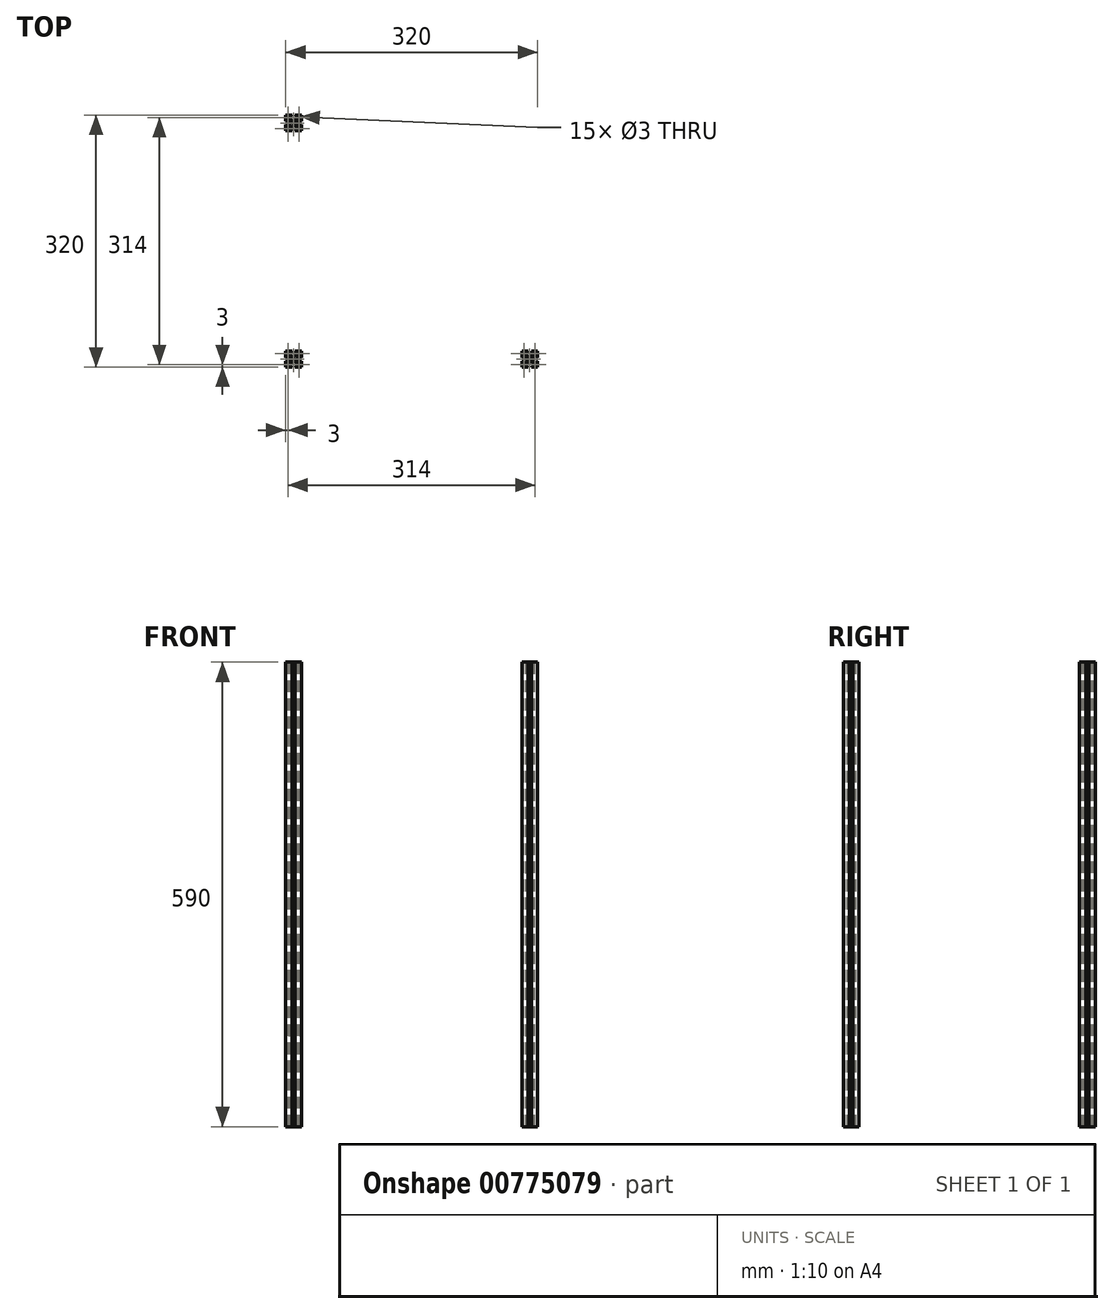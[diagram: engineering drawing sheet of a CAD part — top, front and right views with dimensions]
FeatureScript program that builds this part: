
annotation { "Feature Type Name" : "Feature", "Feature Type Description" : "" }
export const myFeature = defineFeature(function(context is Context, id is Id, definition is map)
    precondition{}
    {
        {
            var Q0;
            Q0=qCreatedBy(makeId("Top.planeOp"),FACE);
            var sketch = newSketch(context, id + "F0", { "sketchPlane" : qUnion([Q0])});
            skLineSegment(sketch, "E0.bottom", {"start": v(-10, 10) * mm, "end": v(-2.15, 10) * mm});
            skLineSegment(sketch, "E0.top", {"start": v(-10, -10) * mm, "end": v(-2.15, -10) * mm});
            skLineSegment(sketch, "E0.left", {"start": v(-10, 10) * mm, "end": v(-10, 2.15) * mm});
            skLineSegment(sketch, "E0.right", {"start": v(10, 10) * mm, "end": v(10, 2.15) * mm});
            skLineSegment(sketch, "E1", {"start": v(-35.32, 0) * mm, "end": v(22.78, 0) * mm, "construction": true});
            skLineSegment(sketch, "E2.0", {"start": v(-10, -7) * mm, "end": v(10, -7) * mm, "construction": true});
            skLineSegment(sketch, "E3.0", {"start": v(-10, 7) * mm, "end": v(10, 7) * mm, "construction": true});
            skLineSegment(sketch, "E4", {"start": v(0, -15.68) * mm, "end": v(0, 21.93) * mm, "construction": true});
            skPoint(sketch, "E4.endSnap0", {"position": v(0, -7) * mm});
            skLineSegment(sketch, "E5.0", {"start": v(7, -10) * mm, "end": v(7, 10) * mm, "construction": true});
            skLineSegment(sketch, "E6.0", {"start": v(-7, -10) * mm, "end": v(-7, 10) * mm, "construction": true});
            skLineSegment(sketch, "E7.0", {"start": v(-4.15, 8.5) * mm, "end": v(-2.15, 8.5) * mm});
            skLineSegment(sketch, "E8.0", {"start": v(-4.15, 4.8) * mm, "end": v(-2.15, 4.8) * mm});
            skLineSegment(sketch, "E9.trimOffspring", {"start": v(2.15, 8.5) * mm, "end": v(2.15, 10) * mm});
            skLineSegment(sketch, "E10.trimOffspring", {"start": v(4.15, 4.8) * mm, "end": v(4.15, 8.5) * mm});
            skLineSegment(sketch, "E11.MirrorCS", {"start": v(-2.15, 8.5) * mm, "end": v(-2.15, 10) * mm});
            skLineSegment(sketch, "E12", {"start": v(-2.15, 3.3) * mm, "end": v(4.15, 4.8) * mm});
            skLineSegment(sketch, "E13.trimOffspring", {"start": v(-2.15, 4.8) * mm, "end": v(-2.15, 3.3) * mm});
            skLineSegment(sketch, "E14.MirrorCS", {"start": v(-4.15, 4.8) * mm, "end": v(-4.15, 8.5) * mm});
            skLineSegment(sketch, "E15.trimOffspring", {"start": v(2.15, 8.5) * mm, "end": v(4.15, 8.5) * mm});
            skLineSegment(sketch, "E16.trimOffspring", {"start": v(2.15, 10) * mm, "end": v(10, 10) * mm});
            skLineSegment(sketch, "E17.1.0", {"start": v(4.8, 4.15) * mm, "end": v(4.8, 2.15) * mm});
            skLineSegment(sketch, "E17.1.1", {"start": v(8.5, 4.15) * mm, "end": v(8.5, 2.15) * mm});
            skLineSegment(sketch, "E17.1.2", {"start": v(3.3, 2.15) * mm, "end": v(4.8, -4.15) * mm});
            skLineSegment(sketch, "E17.1.3", {"start": v(8.5, 2.15) * mm, "end": v(10, 2.15) * mm});
            skLineSegment(sketch, "E17.1.4", {"start": v(4.8, -4.15) * mm, "end": v(8.5, -4.15) * mm});
            skLineSegment(sketch, "E17.1.5", {"start": v(4.8, 4.15) * mm, "end": v(8.5, 4.15) * mm});
            skLineSegment(sketch, "E17.1.6", {"start": v(4.8, 2.15) * mm, "end": v(3.3, 2.15) * mm});
            skLineSegment(sketch, "E17.1.7", {"start": v(8.5, -2.15) * mm, "end": v(8.5, -4.15) * mm});
            skLineSegment(sketch, "E17.1.8", {"start": v(8.5, -2.15) * mm, "end": v(10, -2.15) * mm});
            skLineSegment(sketch, "E17.2.0", {"start": v(4.15, -4.8) * mm, "end": v(2.15, -4.8) * mm});
            skLineSegment(sketch, "E17.2.1", {"start": v(4.15, -8.5) * mm, "end": v(2.15, -8.5) * mm});
            skLineSegment(sketch, "E17.2.2", {"start": v(2.15, -3.3) * mm, "end": v(-4.15, -4.8) * mm});
            skLineSegment(sketch, "E17.2.3", {"start": v(2.15, -8.5) * mm, "end": v(2.15, -10) * mm});
            skLineSegment(sketch, "E17.2.4", {"start": v(-4.15, -4.8) * mm, "end": v(-4.15, -8.5) * mm});
            skLineSegment(sketch, "E17.2.5", {"start": v(4.15, -4.8) * mm, "end": v(4.15, -8.5) * mm});
            skLineSegment(sketch, "E17.2.6", {"start": v(2.15, -4.8) * mm, "end": v(2.15, -3.3) * mm});
            skLineSegment(sketch, "E17.2.7", {"start": v(-2.15, -8.5) * mm, "end": v(-4.15, -8.5) * mm});
            skLineSegment(sketch, "E17.2.8", {"start": v(-2.15, -8.5) * mm, "end": v(-2.15, -10) * mm});
            skPoint(sketch, "E17.center", {"position": v(0, 0) * mm});
            skLineSegment(sketch, "E18.trimOffspring", {"start": v(10, -2.15) * mm, "end": v(10, -10) * mm});
            skLineSegment(sketch, "E19.trimOffspring", {"start": v(2.15, -10) * mm, "end": v(10, -10) * mm});
            skPoint(sketch, "E20.1.7", {"position": v(-4.95, -4.95) * mm});
            skLineSegment(sketch, "E20.2.0", {"start": v(-8.5, 2.15) * mm, "end": v(-10, 2.15) * mm});
            skLineSegment(sketch, "E20.2.1", {"start": v(-8.5, -4.15) * mm, "end": v(-8.5, -2.15) * mm});
            skLineSegment(sketch, "E20.2.2", {"start": v(-4.8, 4.15) * mm, "end": v(-8.5, 4.15) * mm});
            skLineSegment(sketch, "E20.2.3", {"start": v(-4.8, -2.15) * mm, "end": v(-3.3, -2.15) * mm});
            skLineSegment(sketch, "E20.2.4", {"start": v(-8.5, -2.15) * mm, "end": v(-10, -2.15) * mm});
            skLineSegment(sketch, "E20.2.5", {"start": v(-8.5, 2.15) * mm, "end": v(-8.5, 4.15) * mm});
            skLineSegment(sketch, "E20.2.6", {"start": v(-4.8, -4.15) * mm, "end": v(-4.8, -2.15) * mm});
            skPoint(sketch, "E20.2.7", {"position": v(-7, 0) * mm});
            skLineSegment(sketch, "E20.2.8", {"start": v(-3.3, -2.15) * mm, "end": v(-4.8, 4.15) * mm});
            skLineSegment(sketch, "E20.2.9", {"start": v(-4.8, -4.15) * mm, "end": v(-8.5, -4.15) * mm});
            skLineSegment(sketch, "E21.trimOffspring", {"start": v(-10, -2.15) * mm, "end": v(-10, -10) * mm});
            skCircle(sketch, "E22", {"center": v(-7, 7) * mm, "radius": 1.5 * mm});
            skCircle(sketch, "E23", {"center": v(7, 7) * mm, "radius": 1.5 * mm});
            skCircle(sketch, "E24", {"center": v(7, -7) * mm, "radius": 1.5 * mm});
            skCircle(sketch, "E25", {"center": v(-7, -7) * mm, "radius": 1.5 * mm});
            skCircle(sketch, "E26", {"center": v(0, 0) * mm, "radius": 1.5 * mm});
            skSolve(sketch);
        }
        {
            var Q0;
            Q0 = qSketchRegion(id + "F0", true);
            extrude(context, id + "F1", {"entities" : qUnion([Q0]), "depth" : 590 * mm, "offsetDistance" : 25 * mm});
        }
        {
            var Q0;
            Q0=makeQuery(id+"F1.opExtrude","SWEPT_BODY",BODY,{"disambiguationData":[OSD([sQuery(id+"F0.wireOp",EDGE,"E0.bottom"),sQuery(id+"F0.wireOp",EDGE,"E0.top"),sQuery(id+"F0.wireOp",EDGE,"E0.left"),sQuery(id+"F0.wireOp",EDGE,"E0.right"),sQuery(id+"F0.wireOp",EDGE,"E7.0"),sQuery(id+"F0.wireOp",EDGE,"E8.0"),sQuery(id+"F0.wireOp",EDGE,"E9.trimOffspring"),sQuery(id+"F0.wireOp",EDGE,"E10.trimOffspring"),sQuery(id+"F0.wireOp",EDGE,"E11.MirrorCS"),sQuery(id+"F0.wireOp",EDGE,"E12"),sQuery(id+"F0.wireOp",EDGE,"E13.trimOffspring"),sQuery(id+"F0.wireOp",EDGE,"E14.MirrorCS"),sQuery(id+"F0.wireOp",EDGE,"E15.trimOffspring"),sQuery(id+"F0.wireOp",EDGE,"E16.trimOffspring"),sQuery(id+"F0.wireOp",EDGE,"E17.1.0"),sQuery(id+"F0.wireOp",EDGE,"E17.1.1"),sQuery(id+"F0.wireOp",EDGE,"E17.1.2"),sQuery(id+"F0.wireOp",EDGE,"E17.1.3"),sQuery(id+"F0.wireOp",EDGE,"E17.1.4"),sQuery(id+"F0.wireOp",EDGE,"E17.1.5"),sQuery(id+"F0.wireOp",EDGE,"E17.1.6"),sQuery(id+"F0.wireOp",EDGE,"E17.1.7"),sQuery(id+"F0.wireOp",EDGE,"E17.1.8"),sQuery(id+"F0.wireOp",EDGE,"E17.2.0"),sQuery(id+"F0.wireOp",EDGE,"E17.2.1"),sQuery(id+"F0.wireOp",EDGE,"E17.2.2"),sQuery(id+"F0.wireOp",EDGE,"E17.2.3"),sQuery(id+"F0.wireOp",EDGE,"E17.2.4"),sQuery(id+"F0.wireOp",EDGE,"E17.2.5"),sQuery(id+"F0.wireOp",EDGE,"E17.2.6"),sQuery(id+"F0.wireOp",EDGE,"E17.2.7"),sQuery(id+"F0.wireOp",EDGE,"E17.2.8"),sQuery(id+"F0.wireOp",EDGE,"E18.trimOffspring"),sQuery(id+"F0.wireOp",EDGE,"E19.trimOffspring"),sQuery(id+"F0.wireOp",EDGE,"E20.2.0"),sQuery(id+"F0.wireOp",EDGE,"E20.2.1"),sQuery(id+"F0.wireOp",EDGE,"E20.2.2"),sQuery(id+"F0.wireOp",EDGE,"E20.2.3"),sQuery(id+"F0.wireOp",EDGE,"E20.2.4"),sQuery(id+"F0.wireOp",EDGE,"E20.2.5"),sQuery(id+"F0.wireOp",EDGE,"E20.2.6"),sQuery(id+"F0.wireOp",EDGE,"E20.2.8"),sQuery(id+"F0.wireOp",EDGE,"E20.2.9"),sQuery(id+"F0.wireOp",EDGE,"E21.trimOffspring"),sQuery(id+"F0.wireOp",EDGE,"E22"),sQuery(id+"F0.wireOp",EDGE,"E23"),sQuery(id+"F0.wireOp",EDGE,"E24"),sQuery(id+"F0.wireOp",EDGE,"E25"),sQuery(id+"F0.wireOp",EDGE,"E26")])]});
            transform(context, id + "F2", {"entities" : qUnion([Q0]), "transformType" : TransformType.TRANSLATION_3D, "dx" : 0 * mm, "dy" : 0 * mm, "dz" : -300 * mm, "makeCopy" : true});
        }
        {
            var Q0;
            Q0=makeQuery(id+"F2.opPattern","COPY",BODY,{"derivedFrom":makeQuery(id+"F1.opExtrude","SWEPT_BODY",BODY,{"disambiguationData":[OSD([sQuery(id+"F0.wireOp",EDGE,"E0.bottom"),sQuery(id+"F0.wireOp",EDGE,"E0.top"),sQuery(id+"F0.wireOp",EDGE,"E0.left"),sQuery(id+"F0.wireOp",EDGE,"E0.right"),sQuery(id+"F0.wireOp",EDGE,"E7.0"),sQuery(id+"F0.wireOp",EDGE,"E8.0"),sQuery(id+"F0.wireOp",EDGE,"E9.trimOffspring"),sQuery(id+"F0.wireOp",EDGE,"E10.trimOffspring"),sQuery(id+"F0.wireOp",EDGE,"E11.MirrorCS"),sQuery(id+"F0.wireOp",EDGE,"E12"),sQuery(id+"F0.wireOp",EDGE,"E13.trimOffspring"),sQuery(id+"F0.wireOp",EDGE,"E14.MirrorCS"),sQuery(id+"F0.wireOp",EDGE,"E15.trimOffspring"),sQuery(id+"F0.wireOp",EDGE,"E16.trimOffspring"),sQuery(id+"F0.wireOp",EDGE,"E17.1.0"),sQuery(id+"F0.wireOp",EDGE,"E17.1.1"),sQuery(id+"F0.wireOp",EDGE,"E17.1.2"),sQuery(id+"F0.wireOp",EDGE,"E17.1.3"),sQuery(id+"F0.wireOp",EDGE,"E17.1.4"),sQuery(id+"F0.wireOp",EDGE,"E17.1.5"),sQuery(id+"F0.wireOp",EDGE,"E17.1.6"),sQuery(id+"F0.wireOp",EDGE,"E17.1.7"),sQuery(id+"F0.wireOp",EDGE,"E17.1.8"),sQuery(id+"F0.wireOp",EDGE,"E17.2.0"),sQuery(id+"F0.wireOp",EDGE,"E17.2.1"),sQuery(id+"F0.wireOp",EDGE,"E17.2.2"),sQuery(id+"F0.wireOp",EDGE,"E17.2.3"),sQuery(id+"F0.wireOp",EDGE,"E17.2.4"),sQuery(id+"F0.wireOp",EDGE,"E17.2.5"),sQuery(id+"F0.wireOp",EDGE,"E17.2.6"),sQuery(id+"F0.wireOp",EDGE,"E17.2.7"),sQuery(id+"F0.wireOp",EDGE,"E17.2.8"),sQuery(id+"F0.wireOp",EDGE,"E18.trimOffspring"),sQuery(id+"F0.wireOp",EDGE,"E19.trimOffspring"),sQuery(id+"F0.wireOp",EDGE,"E20.2.0"),sQuery(id+"F0.wireOp",EDGE,"E20.2.1"),sQuery(id+"F0.wireOp",EDGE,"E20.2.2"),sQuery(id+"F0.wireOp",EDGE,"E20.2.3"),sQuery(id+"F0.wireOp",EDGE,"E20.2.4"),sQuery(id+"F0.wireOp",EDGE,"E20.2.5"),sQuery(id+"F0.wireOp",EDGE,"E20.2.6"),sQuery(id+"F0.wireOp",EDGE,"E20.2.8"),sQuery(id+"F0.wireOp",EDGE,"E20.2.9"),sQuery(id+"F0.wireOp",EDGE,"E21.trimOffspring"),sQuery(id+"F0.wireOp",EDGE,"E22"),sQuery(id+"F0.wireOp",EDGE,"E23"),sQuery(id+"F0.wireOp",EDGE,"E24"),sQuery(id+"F0.wireOp",EDGE,"E25"),sQuery(id+"F0.wireOp",EDGE,"E26")])]}),"instanceName":"1"});
            deleteBodies(context, id + "F3", {"entities" : qUnion([Q0])});
        }
        {
            var Q0;
            Q0=makeQuery(id+"F1.opExtrude","SWEPT_BODY",BODY,{"disambiguationData":[OSD([sQuery(id+"F0.wireOp",EDGE,"E0.bottom"),sQuery(id+"F0.wireOp",EDGE,"E0.top"),sQuery(id+"F0.wireOp",EDGE,"E0.left"),sQuery(id+"F0.wireOp",EDGE,"E0.right"),sQuery(id+"F0.wireOp",EDGE,"E7.0"),sQuery(id+"F0.wireOp",EDGE,"E8.0"),sQuery(id+"F0.wireOp",EDGE,"E9.trimOffspring"),sQuery(id+"F0.wireOp",EDGE,"E10.trimOffspring"),sQuery(id+"F0.wireOp",EDGE,"E11.MirrorCS"),sQuery(id+"F0.wireOp",EDGE,"E12"),sQuery(id+"F0.wireOp",EDGE,"E13.trimOffspring"),sQuery(id+"F0.wireOp",EDGE,"E14.MirrorCS"),sQuery(id+"F0.wireOp",EDGE,"E15.trimOffspring"),sQuery(id+"F0.wireOp",EDGE,"E16.trimOffspring"),sQuery(id+"F0.wireOp",EDGE,"E17.1.0"),sQuery(id+"F0.wireOp",EDGE,"E17.1.1"),sQuery(id+"F0.wireOp",EDGE,"E17.1.2"),sQuery(id+"F0.wireOp",EDGE,"E17.1.3"),sQuery(id+"F0.wireOp",EDGE,"E17.1.4"),sQuery(id+"F0.wireOp",EDGE,"E17.1.5"),sQuery(id+"F0.wireOp",EDGE,"E17.1.6"),sQuery(id+"F0.wireOp",EDGE,"E17.1.7"),sQuery(id+"F0.wireOp",EDGE,"E17.1.8"),sQuery(id+"F0.wireOp",EDGE,"E17.2.0"),sQuery(id+"F0.wireOp",EDGE,"E17.2.1"),sQuery(id+"F0.wireOp",EDGE,"E17.2.2"),sQuery(id+"F0.wireOp",EDGE,"E17.2.3"),sQuery(id+"F0.wireOp",EDGE,"E17.2.4"),sQuery(id+"F0.wireOp",EDGE,"E17.2.5"),sQuery(id+"F0.wireOp",EDGE,"E17.2.6"),sQuery(id+"F0.wireOp",EDGE,"E17.2.7"),sQuery(id+"F0.wireOp",EDGE,"E17.2.8"),sQuery(id+"F0.wireOp",EDGE,"E18.trimOffspring"),sQuery(id+"F0.wireOp",EDGE,"E19.trimOffspring"),sQuery(id+"F0.wireOp",EDGE,"E20.2.0"),sQuery(id+"F0.wireOp",EDGE,"E20.2.1"),sQuery(id+"F0.wireOp",EDGE,"E20.2.2"),sQuery(id+"F0.wireOp",EDGE,"E20.2.3"),sQuery(id+"F0.wireOp",EDGE,"E20.2.4"),sQuery(id+"F0.wireOp",EDGE,"E20.2.5"),sQuery(id+"F0.wireOp",EDGE,"E20.2.6"),sQuery(id+"F0.wireOp",EDGE,"E20.2.8"),sQuery(id+"F0.wireOp",EDGE,"E20.2.9"),sQuery(id+"F0.wireOp",EDGE,"E21.trimOffspring"),sQuery(id+"F0.wireOp",EDGE,"E22"),sQuery(id+"F0.wireOp",EDGE,"E23"),sQuery(id+"F0.wireOp",EDGE,"E24"),sQuery(id+"F0.wireOp",EDGE,"E25"),sQuery(id+"F0.wireOp",EDGE,"E26")])]});
            transform(context, id + "F4", {"entities" : qUnion([Q0]), "transformType" : TransformType.TRANSLATION_3D, "dx" : 0 * mm, "dy" : 300 * mm, "dz" : 0 * mm, "makeCopy" : true});
        }
        {
            var Q0;
            Q0=makeQuery(id+"F1.opExtrude","SWEPT_BODY",BODY,{"disambiguationData":[OSD([sQuery(id+"F0.wireOp",EDGE,"E0.bottom"),sQuery(id+"F0.wireOp",EDGE,"E0.top"),sQuery(id+"F0.wireOp",EDGE,"E0.left"),sQuery(id+"F0.wireOp",EDGE,"E0.right"),sQuery(id+"F0.wireOp",EDGE,"E7.0"),sQuery(id+"F0.wireOp",EDGE,"E8.0"),sQuery(id+"F0.wireOp",EDGE,"E9.trimOffspring"),sQuery(id+"F0.wireOp",EDGE,"E10.trimOffspring"),sQuery(id+"F0.wireOp",EDGE,"E11.MirrorCS"),sQuery(id+"F0.wireOp",EDGE,"E12"),sQuery(id+"F0.wireOp",EDGE,"E13.trimOffspring"),sQuery(id+"F0.wireOp",EDGE,"E14.MirrorCS"),sQuery(id+"F0.wireOp",EDGE,"E15.trimOffspring"),sQuery(id+"F0.wireOp",EDGE,"E16.trimOffspring"),sQuery(id+"F0.wireOp",EDGE,"E17.1.0"),sQuery(id+"F0.wireOp",EDGE,"E17.1.1"),sQuery(id+"F0.wireOp",EDGE,"E17.1.2"),sQuery(id+"F0.wireOp",EDGE,"E17.1.3"),sQuery(id+"F0.wireOp",EDGE,"E17.1.4"),sQuery(id+"F0.wireOp",EDGE,"E17.1.5"),sQuery(id+"F0.wireOp",EDGE,"E17.1.6"),sQuery(id+"F0.wireOp",EDGE,"E17.1.7"),sQuery(id+"F0.wireOp",EDGE,"E17.1.8"),sQuery(id+"F0.wireOp",EDGE,"E17.2.0"),sQuery(id+"F0.wireOp",EDGE,"E17.2.1"),sQuery(id+"F0.wireOp",EDGE,"E17.2.2"),sQuery(id+"F0.wireOp",EDGE,"E17.2.3"),sQuery(id+"F0.wireOp",EDGE,"E17.2.4"),sQuery(id+"F0.wireOp",EDGE,"E17.2.5"),sQuery(id+"F0.wireOp",EDGE,"E17.2.6"),sQuery(id+"F0.wireOp",EDGE,"E17.2.7"),sQuery(id+"F0.wireOp",EDGE,"E17.2.8"),sQuery(id+"F0.wireOp",EDGE,"E18.trimOffspring"),sQuery(id+"F0.wireOp",EDGE,"E19.trimOffspring"),sQuery(id+"F0.wireOp",EDGE,"E20.2.0"),sQuery(id+"F0.wireOp",EDGE,"E20.2.1"),sQuery(id+"F0.wireOp",EDGE,"E20.2.2"),sQuery(id+"F0.wireOp",EDGE,"E20.2.3"),sQuery(id+"F0.wireOp",EDGE,"E20.2.4"),sQuery(id+"F0.wireOp",EDGE,"E20.2.5"),sQuery(id+"F0.wireOp",EDGE,"E20.2.6"),sQuery(id+"F0.wireOp",EDGE,"E20.2.8"),sQuery(id+"F0.wireOp",EDGE,"E20.2.9"),sQuery(id+"F0.wireOp",EDGE,"E21.trimOffspring"),sQuery(id+"F0.wireOp",EDGE,"E22"),sQuery(id+"F0.wireOp",EDGE,"E23"),sQuery(id+"F0.wireOp",EDGE,"E24"),sQuery(id+"F0.wireOp",EDGE,"E25"),sQuery(id+"F0.wireOp",EDGE,"E26")])]});
            transform(context, id + "F5", {"entities" : qUnion([Q0]), "transformType" : TransformType.TRANSLATION_3D, "dx" : 300 * mm, "dy" : 0 * mm, "dz" : 0 * mm, "makeCopy" : true});
        }
    });
